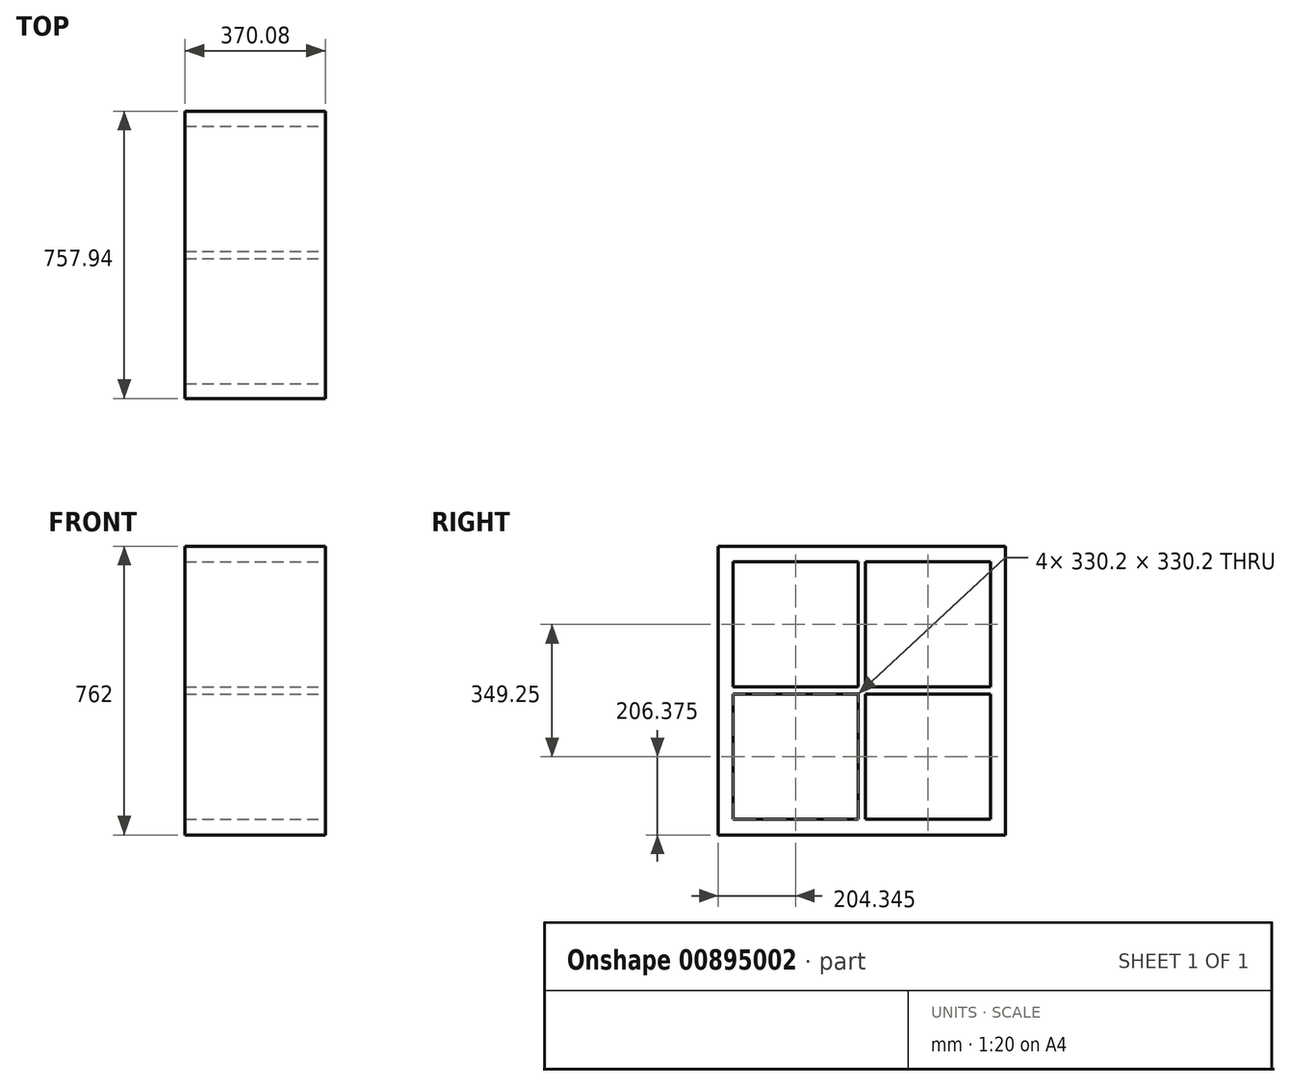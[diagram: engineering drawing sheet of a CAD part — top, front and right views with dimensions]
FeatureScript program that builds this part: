
annotation { "Feature Type Name" : "Feature", "Feature Type Description" : "" }
export const myFeature = defineFeature(function(context is Context, id is Id, definition is map)
    precondition{}
    {
        {
            var Q0;
            Q0=qCreatedBy(makeId("Right.planeOp"),FACE);
            var sketch = newSketch(context, id + "F0", { "sketchPlane" : qUnion([Q0])});
            skLineSegment(sketch, "E0.bottom", {"start": v(-378.97, 381) * mm, "end": v(378.97, 381) * mm});
            skLineSegment(sketch, "E0.top", {"start": v(-378.97, -381) * mm, "end": v(378.97, -381) * mm});
            skLineSegment(sketch, "E0.left", {"start": v(-378.97, 381) * mm, "end": v(-378.97, -381) * mm});
            skLineSegment(sketch, "E0.right", {"start": v(378.97, 381) * mm, "end": v(378.97, -381) * mm});
            skPoint(sketch, "E0.middle", {"position": v(0, 0) * mm});
            skSolve(sketch);
        }
        {
            var Q0;
            Q0 = qSketchRegion(id + "F0", true);
            extrude(context, id + "F1", {"entities" : qUnion([Q0]), "oppositeDirection" : true, "depth" : 370.08 * mm, "offsetDistance" : 25.4 * mm});
        }
        {
            var Q0;
            Q0=makeQuery(id+"F1.opExtrude","CAP_FACE",FACE,{"disambiguationData":[OSD([sQuery(id+"F0.wireOp",EDGE,"E0.bottom"),sQuery(id+"F0.wireOp",EDGE,"E0.top"),sQuery(id+"F0.wireOp",EDGE,"E0.left"),sQuery(id+"F0.wireOp",EDGE,"E0.right")])],"isStart":true});
            var sketch = newSketch(context, id + "F2", { "sketchPlane" : qUnion([Q0])});
            skLineSegment(sketch, "E1.bottom", {"start": v(-9.53, 9.52) * mm, "end": v(-339.73, 9.52) * mm});
            skLineSegment(sketch, "E1.top", {"start": v(-9.53, 339.73) * mm, "end": v(-339.73, 339.72) * mm});
            skLineSegment(sketch, "E1.left", {"start": v(-9.52, 9.52) * mm, "end": v(-9.53, 339.73) * mm});
            skLineSegment(sketch, "E1.right", {"start": v(-339.73, 9.52) * mm, "end": v(-339.73, 339.72) * mm});
            skLineSegment(sketch, "E2.bottom", {"start": v(9.52, 339.73) * mm, "end": v(339.73, 339.73) * mm});
            skLineSegment(sketch, "E2.top", {"start": v(9.52, 9.53) * mm, "end": v(339.73, 9.53) * mm});
            skLineSegment(sketch, "E2.left", {"start": v(9.52, 339.73) * mm, "end": v(9.52, 9.53) * mm});
            skLineSegment(sketch, "E2.right", {"start": v(339.73, 339.73) * mm, "end": v(339.73, 9.53) * mm});
            skLineSegment(sketch, "E3.bottom", {"start": v(339.73, -9.52) * mm, "end": v(9.52, -9.52) * mm});
            skLineSegment(sketch, "E3.top", {"start": v(339.73, -339.73) * mm, "end": v(9.52, -339.73) * mm});
            skLineSegment(sketch, "E3.left", {"start": v(339.73, -9.52) * mm, "end": v(339.73, -339.73) * mm});
            skLineSegment(sketch, "E3.right", {"start": v(9.52, -9.52) * mm, "end": v(9.53, -339.73) * mm});
            skLineSegment(sketch, "E4.bottom", {"start": v(-9.52, -339.73) * mm, "end": v(-339.73, -339.73) * mm});
            skLineSegment(sketch, "E4.top", {"start": v(-9.53, -9.53) * mm, "end": v(-339.73, -9.53) * mm});
            skLineSegment(sketch, "E4.left", {"start": v(-9.52, -339.73) * mm, "end": v(-9.52, -9.53) * mm});
            skLineSegment(sketch, "E4.right", {"start": v(-339.73, -339.73) * mm, "end": v(-339.73, -9.53) * mm});
            skSolve(sketch);
        }
        {
            var Q0;
            Q0 = qSketchRegion(id + "F2", true);
            extrude(context, id + "F3", {"entities" : qUnion([Q0]), "operationType" : NewBodyOperationType.REMOVE, "endBound" : BoundingType.THROUGH_ALL, "oppositeDirection" : true, "depth" : 25.4 * mm, "offsetDistance" : 25.4 * mm});
        }
    });
